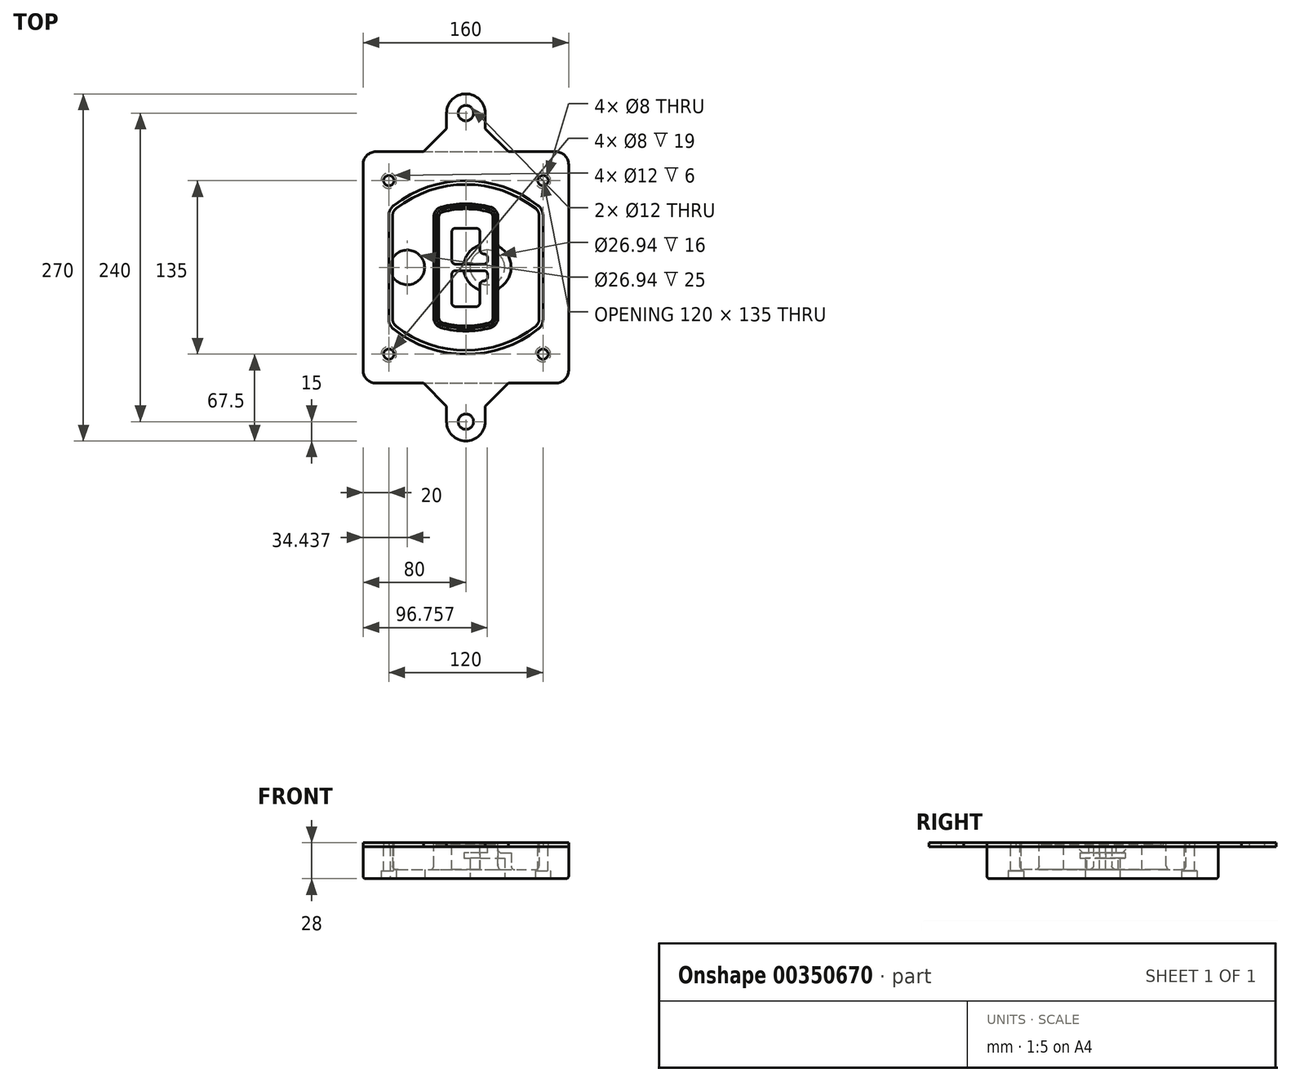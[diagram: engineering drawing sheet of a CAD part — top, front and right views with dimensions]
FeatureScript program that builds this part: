
annotation { "Feature Type Name" : "Feature", "Feature Type Description" : "" }
export const myFeature = defineFeature(function(context is Context, id is Id, definition is map)
    precondition{}
    {
        {
            var Q0;
            Q0=qCreatedBy(makeId("Top.planeOp"),FACE);
            var sketch = newSketch(context, id + "F0", { "sketchPlane" : qUnion([Q0])});
            skPoint(sketch, "E0.rect.middle", {"position": v(0, 0) * mm});
            skLineSegment(sketch, "E1.bottom", {"start": v(-70, -90) * mm, "end": v(70, -90) * mm});
            skLineSegment(sketch, "E1.top", {"start": v(-70, 90) * mm, "end": v(70, 90) * mm});
            skLineSegment(sketch, "E1.left", {"start": v(-80, -80) * mm, "end": v(-80, 80) * mm});
            skLineSegment(sketch, "E1.right", {"start": v(80, -80) * mm, "end": v(80, 80) * mm});
            skLineSegment(sketch, "E2", {"start": v(-80, 90) * mm, "end": v(80, -90) * mm, "construction": true});
            skLineSegment(sketch, "E3", {"start": v(80, 90) * mm, "end": v(-80, -90) * mm, "construction": true});
            skCircle(sketch, "E4", {"center": v(-60, 67.5) * mm, "radius": 4 * mm});
            skCircle(sketch, "E5", {"center": v(60, 67.5) * mm, "radius": 4 * mm});
            skCircle(sketch, "E6", {"center": v(60, -67.5) * mm, "radius": 4 * mm});
            skCircle(sketch, "E7", {"center": v(-60, -67.5) * mm, "radius": 4 * mm});
            skLineSegment(sketch, "E8", {"start": v(-60, 67.5) * mm, "end": v(60, 67.5) * mm, "construction": true});
            skLineSegment(sketch, "E9", {"start": v(60, 67.5) * mm, "end": v(60, -67.5) * mm, "construction": true});
            skLineSegment(sketch, "E10", {"start": v(60, -67.5) * mm, "end": v(-60, -67.5) * mm, "construction": true});
            skLineSegment(sketch, "E11", {"start": v(-60, -67.5) * mm, "end": v(-60, 67.5) * mm, "construction": true});
            skLineSegment(sketch, "E12", {"start": v(-60, 40.3) * mm, "end": v(-60, -40.3) * mm});
            skLineSegment(sketch, "E13", {"start": v(60, 40.3) * mm, "end": v(60, -40.3) * mm});
            skArc(sketch, "E14", {"start": v(56.15, 48.18) * mm, "mid": v(0, 67.5) * mm, "end": v(-56.15, 48.18) * mm});
            skArc(sketch, "E15", {"start": v(-56.15, -48.18) * mm, "mid": v(0, -67.5) * mm, "end": v(56.15, -48.18) * mm});
            skLineSegment(sketch, "E16", {"start": v(-60, 0) * mm, "end": v(60, 0) * mm, "construction": true});
            skPoint(sketch, "E17.visualSharp", {"position": v(-60, -45) * mm});
            skArc(sketch, "E17.filletArc", {"start": v(-60, -40.3) * mm, "mid": v(-58.99, -44.68) * mm, "end": v(-56.15, -48.18) * mm});
            skPoint(sketch, "E18.visualSharp", {"position": v(-60, 45) * mm});
            skArc(sketch, "E18.filletArc", {"start": v(-56.15, 48.18) * mm, "mid": v(-58.99, 44.68) * mm, "end": v(-60, 40.3) * mm});
            skPoint(sketch, "E19.visualSharp", {"position": v(60, 45) * mm});
            skArc(sketch, "E19.filletArc", {"start": v(60, 40.3) * mm, "mid": v(58.99, 44.68) * mm, "end": v(56.15, 48.18) * mm});
            skPoint(sketch, "E20.visualSharp", {"position": v(60, -45) * mm});
            skArc(sketch, "E20.filletArc", {"start": v(56.15, -48.18) * mm, "mid": v(58.99, -44.68) * mm, "end": v(60, -40.3) * mm});
            skPoint(sketch, "E21.visualSharp", {"position": v(-80, 90) * mm});
            skArc(sketch, "E21.filletArc", {"start": v(-70, 90) * mm, "mid": v(-77.07, 87.07) * mm, "end": v(-80, 80) * mm});
            skPoint(sketch, "E22.visualSharp", {"position": v(80, 90) * mm});
            skArc(sketch, "E22.filletArc", {"start": v(80, 80) * mm, "mid": v(77.07, 87.07) * mm, "end": v(70, 90) * mm});
            skPoint(sketch, "E23.visualSharp", {"position": v(80, -90) * mm});
            skArc(sketch, "E23.filletArc", {"start": v(70, -90) * mm, "mid": v(77.07, -87.07) * mm, "end": v(80, -80) * mm});
            skPoint(sketch, "E24.visualSharp", {"position": v(-80, -90) * mm});
            skArc(sketch, "E24.filletArc", {"start": v(-80, -80) * mm, "mid": v(-77.07, -87.07) * mm, "end": v(-70, -90) * mm});
            skArc(sketch, "E25.0", {"start": v(57, 40.3) * mm, "mid": v(56.3, 43.36) * mm, "end": v(54.3, 45.81) * mm});
            skLineSegment(sketch, "E25.1", {"start": v(57, 40.3) * mm, "end": v(57, -40.3) * mm});
            skArc(sketch, "E25.2", {"start": v(54.3, -45.81) * mm, "mid": v(56.3, -43.36) * mm, "end": v(57, -40.3) * mm});
            skArc(sketch, "E25.3", {"start": v(-54.3, -45.81) * mm, "mid": v(0, -64.5) * mm, "end": v(54.3, -45.81) * mm});
            skArc(sketch, "E25.4", {"start": v(-57, -40.3) * mm, "mid": v(-56.3, -43.36) * mm, "end": v(-54.3, -45.81) * mm});
            skArc(sketch, "E25.5", {"start": v(54.3, 45.81) * mm, "mid": v(0, 64.5) * mm, "end": v(-54.3, 45.81) * mm});
            skLineSegment(sketch, "E25.6", {"start": v(-57, 40.3) * mm, "end": v(-57, -40.3) * mm});
            skArc(sketch, "E25.7", {"start": v(-54.3, 45.81) * mm, "mid": v(-56.3, 43.36) * mm, "end": v(-57, 40.3) * mm});
            skArc(sketch, "E26.0", {"start": v(-58.62, 51.33) * mm, "mid": v(-62.58, 46.43) * mm, "end": v(-64, 40.3) * mm});
            skArc(sketch, "E26.1", {"start": v(58.62, 51.33) * mm, "mid": v(0, 71.5) * mm, "end": v(-58.62, 51.33) * mm});
            skArc(sketch, "E26.2", {"start": v(64, 40.3) * mm, "mid": v(62.58, 46.43) * mm, "end": v(58.62, 51.33) * mm});
            skLineSegment(sketch, "E26.3", {"start": v(64, 40.3) * mm, "end": v(64, -40.3) * mm});
            skArc(sketch, "E26.4", {"start": v(58.62, -51.33) * mm, "mid": v(62.58, -46.43) * mm, "end": v(64, -40.3) * mm});
            skLineSegment(sketch, "E26.5", {"start": v(-64, 40.3) * mm, "end": v(-64, -40.3) * mm});
            skArc(sketch, "E26.6", {"start": v(-58.62, -51.33) * mm, "mid": v(0, -71.5) * mm, "end": v(58.62, -51.33) * mm});
            skArc(sketch, "E26.7", {"start": v(-64, -40.3) * mm, "mid": v(-62.58, -46.43) * mm, "end": v(-58.62, -51.33) * mm});
            skSolve(sketch);
        }
        {
            var Q0;
            Q0=makeQuery(id+"F0.imprint","IMPRINT",FACE,{"disambiguationData":[TD([[makeQuery(id+"F0.imprint","IMPRINT",EDGE,{"derivedFrom":sQuery(id+"F0.wireOp",EDGE,"E1.bottom")}),1.0]])]});
            var Q1;
            Q1=makeQuery(id+"F0.imprint","IMPRINT",FACE,{"disambiguationData":[TD([[makeQuery(id+"F0.imprint","IMPRINT",EDGE,{"derivedFrom":sQuery(id+"F0.wireOp",EDGE,"E12")}),1.0]])]});
            var Q2;
            Q2=makeQuery(id+"F0.imprint","IMPRINT",FACE,{"disambiguationData":[TD([[makeQuery(id+"F0.imprint","IMPRINT",EDGE,{"derivedFrom":sQuery(id+"F0.wireOp",EDGE,"E25.0")}),1.0]])]});
            var Q3;
            Q3=makeQuery(id+"F0.imprint","IMPRINT",FACE,{"disambiguationData":[TD([[makeQuery(id+"F0.imprint","IMPRINT",EDGE,{"derivedFrom":sQuery(id+"F0.wireOp",EDGE,"E12")}),-1.0]])]});
            extrude(context, id + "F1", {"entities" : qUnion([Q0, Q1, Q2, Q3]), "oppositeDirection" : true, "depth" : 25 * mm});
        }
        {
            var Q0;
            Q0=makeQuery(id+"F0.imprint","IMPRINT",FACE,{"disambiguationData":[TD([[makeQuery(id+"F0.imprint","IMPRINT",EDGE,{"derivedFrom":sQuery(id+"F0.wireOp",EDGE,"E12")}),1.0]])]});
            extrude(context, id + "F2", {"entities" : qUnion([Q0]), "operationType" : NewBodyOperationType.ADD, "depth" : 3 * mm});
        }
        {
            var Q0;
            Q0=makeQuery(id+"F0.imprint","IMPRINT",FACE,{"disambiguationData":[TD([[makeQuery(id+"F0.imprint","IMPRINT",EDGE,{"derivedFrom":sQuery(id+"F0.wireOp",EDGE,"E25.0")}),1.0]])]});
            extrude(context, id + "F3", {"entities" : qUnion([Q0]), "operationType" : NewBodyOperationType.REMOVE, "oppositeDirection" : true, "depth" : 18 * mm});
        }
        {
            var Q0;
            Q0=makeQuery(id+"F2.opExtrude","CAP_FACE",FACE,{"disambiguationData":[OSD([sQuery(id+"F0.wireOp",EDGE,"E12"),sQuery(id+"F0.wireOp",EDGE,"E13"),sQuery(id+"F0.wireOp",EDGE,"E14"),sQuery(id+"F0.wireOp",EDGE,"E15"),sQuery(id+"F0.wireOp",EDGE,"E17.filletArc"),sQuery(id+"F0.wireOp",EDGE,"E18.filletArc"),sQuery(id+"F0.wireOp",EDGE,"E19.filletArc"),sQuery(id+"F0.wireOp",EDGE,"E20.filletArc"),sQuery(id+"F0.wireOp",EDGE,"E25.0"),sQuery(id+"F0.wireOp",EDGE,"E25.1"),sQuery(id+"F0.wireOp",EDGE,"E25.2"),sQuery(id+"F0.wireOp",EDGE,"E25.3"),sQuery(id+"F0.wireOp",EDGE,"E25.4"),sQuery(id+"F0.wireOp",EDGE,"E25.5"),sQuery(id+"F0.wireOp",EDGE,"E25.6"),sQuery(id+"F0.wireOp",EDGE,"E25.7")])],"isStart":false});
            var sketch = newSketch(context, id + "F4", { "sketchPlane" : qUnion([Q0])});
            skArc(sketch, "E27.0", {"start": v(-19.08, -46.97) * mm, "mid": v(0, -49.5) * mm, "end": v(19.08, -46.97) * mm});
            skArc(sketch, "E28.0", {"start": v(19.08, 46.97) * mm, "mid": v(0, 49.5) * mm, "end": v(-19.08, 46.97) * mm});
            skLineSegment(sketch, "E29", {"start": v(-25, 39.25) * mm, "end": v(-25, -39.25) * mm});
            skLineSegment(sketch, "E30", {"start": v(25, 39.25) * mm, "end": v(25, -39.25) * mm});
            skLineSegment(sketch, "E31", {"start": v(-25, 45.1) * mm, "end": v(25, 45.1) * mm, "construction": true});
            skLineSegment(sketch, "E32", {"start": v(-25, -45.1) * mm, "end": v(25, -45.1) * mm, "construction": true});
            skPoint(sketch, "E33.visualSharp", {"position": v(-25, 45.1) * mm});
            skArc(sketch, "E33.filletArc", {"start": v(-19.08, 46.97) * mm, "mid": v(-23.35, 44.11) * mm, "end": v(-25, 39.25) * mm});
            skPoint(sketch, "E34.visualSharp", {"position": v(25, 45.1) * mm});
            skArc(sketch, "E34.filletArc", {"start": v(25, 39.25) * mm, "mid": v(23.35, 44.11) * mm, "end": v(19.08, 46.97) * mm});
            skPoint(sketch, "E35.visualSharp", {"position": v(25, -45.1) * mm});
            skArc(sketch, "E35.filletArc", {"start": v(19.08, -46.97) * mm, "mid": v(23.35, -44.11) * mm, "end": v(25, -39.25) * mm});
            skPoint(sketch, "E36.visualSharp", {"position": v(-25, -45.1) * mm});
            skArc(sketch, "E36.filletArc", {"start": v(-25, -39.25) * mm, "mid": v(-23.35, -44.11) * mm, "end": v(-19.08, -46.97) * mm});
            skArc(sketch, "E37.0", {"start": v(54.3, 45.81) * mm, "mid": v(0, 64.5) * mm, "end": v(-54.3, 45.81) * mm});
            skArc(sketch, "E37.1", {"start": v(-54.3, 45.81) * mm, "mid": v(-56.3, 43.36) * mm, "end": v(-57, 40.3) * mm});
            skLineSegment(sketch, "E37.2", {"start": v(-57, 40.3) * mm, "end": v(-57, -40.3) * mm});
            skArc(sketch, "E37.3", {"start": v(-57, -40.3) * mm, "mid": v(-56.3, -43.36) * mm, "end": v(-54.3, -45.81) * mm});
            skArc(sketch, "E37.4", {"start": v(-54.3, -45.81) * mm, "mid": v(0, -64.5) * mm, "end": v(54.3, -45.81) * mm});
            skArc(sketch, "E37.5", {"start": v(54.3, -45.81) * mm, "mid": v(56.3, -43.36) * mm, "end": v(57, -40.3) * mm});
            skLineSegment(sketch, "E37.6", {"start": v(57, 40.3) * mm, "end": v(57, -40.3) * mm});
            skArc(sketch, "E37.7", {"start": v(57, 40.3) * mm, "mid": v(56.3, 43.36) * mm, "end": v(54.3, 45.81) * mm});
            skLineSegment(sketch, "E38.0", {"start": v(23, 39.25) * mm, "end": v(23, -39.25) * mm});
            skArc(sketch, "E38.1", {"start": v(18.56, -45.04) * mm, "mid": v(21.76, -42.9) * mm, "end": v(23, -39.25) * mm});
            skArc(sketch, "E38.2", {"start": v(-18.56, -45.04) * mm, "mid": v(0, -47.5) * mm, "end": v(18.56, -45.04) * mm});
            skArc(sketch, "E38.3", {"start": v(-23, -39.25) * mm, "mid": v(-21.76, -42.9) * mm, "end": v(-18.56, -45.04) * mm});
            skLineSegment(sketch, "E38.4", {"start": v(-23, 39.25) * mm, "end": v(-23, -39.25) * mm});
            skArc(sketch, "E38.5", {"start": v(23, 39.25) * mm, "mid": v(21.76, 42.9) * mm, "end": v(18.56, 45.04) * mm});
            skArc(sketch, "E38.6", {"start": v(-18.56, 45.04) * mm, "mid": v(-21.76, 42.9) * mm, "end": v(-23, 39.25) * mm});
            skArc(sketch, "E38.7", {"start": v(18.56, 45.04) * mm, "mid": v(0, 47.5) * mm, "end": v(-18.56, 45.04) * mm});
            skArc(sketch, "E39.0", {"start": v(21, 39.25) * mm, "mid": v(20.18, 41.68) * mm, "end": v(18.04, 43.1) * mm});
            skLineSegment(sketch, "E39.1", {"start": v(21, 39.25) * mm, "end": v(21, -39.25) * mm});
            skArc(sketch, "E39.2", {"start": v(18.04, -43.1) * mm, "mid": v(20.18, -41.68) * mm, "end": v(21, -39.25) * mm});
            skArc(sketch, "E39.3", {"start": v(-18.04, -43.1) * mm, "mid": v(0, -45.5) * mm, "end": v(18.04, -43.1) * mm});
            skArc(sketch, "E39.4", {"start": v(-21, -39.25) * mm, "mid": v(-20.18, -41.68) * mm, "end": v(-18.04, -43.1) * mm});
            skArc(sketch, "E39.5", {"start": v(18.04, 43.1) * mm, "mid": v(0, 45.5) * mm, "end": v(-18.04, 43.1) * mm});
            skLineSegment(sketch, "E39.6", {"start": v(-21, 39.25) * mm, "end": v(-21, -39.25) * mm});
            skArc(sketch, "E39.7", {"start": v(-18.04, 43.1) * mm, "mid": v(-20.18, 41.68) * mm, "end": v(-21, 39.25) * mm});
            skLineSegment(sketch, "E40", {"start": v(-25, 0) * mm, "end": v(25, 0) * mm, "construction": true});
            skLineSegment(sketch, "E41", {"start": v(-11, 5.5) * mm, "end": v(-11, 27.5) * mm});
            skLineSegment(sketch, "E42", {"start": v(-8, 30.5) * mm, "end": v(8, 30.5) * mm});
            skLineSegment(sketch, "E43", {"start": v(11, 27.5) * mm, "end": v(11, 13.5) * mm});
            skLineSegment(sketch, "E44", {"start": v(14, 10.5) * mm, "end": v(14, 10.5) * mm});
            skLineSegment(sketch, "E45", {"start": v(17, 7.5) * mm, "end": v(17, 5.5) * mm});
            skLineSegment(sketch, "E46", {"start": v(14, 2.5) * mm, "end": v(-8, 2.5) * mm});
            skPoint(sketch, "E47.visualSharp", {"position": v(-11, 30.5) * mm});
            skArc(sketch, "E47.filletArc", {"start": v(-8, 30.5) * mm, "mid": v(-10.12, 29.62) * mm, "end": v(-11, 27.5) * mm});
            skPoint(sketch, "E48.visualSharp", {"position": v(11, 30.5) * mm});
            skArc(sketch, "E48.filletArc", {"start": v(11, 27.5) * mm, "mid": v(10.12, 29.62) * mm, "end": v(8, 30.5) * mm});
            skPoint(sketch, "E49.visualSharp", {"position": v(11, 10.5) * mm});
            skArc(sketch, "E49.filletArc", {"start": v(11, 13.5) * mm, "mid": v(11.88, 11.38) * mm, "end": v(14, 10.5) * mm});
            skPoint(sketch, "E50.visualSharp", {"position": v(17, 10.5) * mm});
            skArc(sketch, "E50.filletArc", {"start": v(17, 7.5) * mm, "mid": v(16.12, 9.62) * mm, "end": v(14, 10.5) * mm});
            skPoint(sketch, "E51.visualSharp", {"position": v(17, 2.5) * mm});
            skArc(sketch, "E51.filletArc", {"start": v(14, 2.5) * mm, "mid": v(16.12, 3.38) * mm, "end": v(17, 5.5) * mm});
            skPoint(sketch, "E52.visualSharp", {"position": v(-11, 2.5) * mm});
            skArc(sketch, "E52.filletArc", {"start": v(-11, 5.5) * mm, "mid": v(-10.12, 3.38) * mm, "end": v(-8, 2.5) * mm});
            skLineSegment(sketch, "E53.0.MirrorCS", {"start": v(14, -2.5) * mm, "end": v(-8, -2.5) * mm});
            skArc(sketch, "E54.0.MirrorCS", {"start": v(-11, -5.5) * mm, "mid": v(-10.12, -3.38) * mm, "end": v(-8, -2.5) * mm});
            skLineSegment(sketch, "E55.0.MirrorCS", {"start": v(-11, -5.5) * mm, "end": v(-11, -27.5) * mm});
            skArc(sketch, "E56.0.MirrorCS", {"start": v(-8, -30.5) * mm, "mid": v(-10.12, -29.62) * mm, "end": v(-11, -27.5) * mm});
            skLineSegment(sketch, "E57.0.MirrorCS", {"start": v(-8, -30.5) * mm, "end": v(8, -30.5) * mm});
            skArc(sketch, "E58.0.MirrorCS", {"start": v(11, -27.5) * mm, "mid": v(10.12, -29.62) * mm, "end": v(8, -30.5) * mm});
            skLineSegment(sketch, "E59.0.MirrorCS", {"start": v(11, -27.5) * mm, "end": v(11, -13.5) * mm});
            skArc(sketch, "E60.0.MirrorCS", {"start": v(11, -13.5) * mm, "mid": v(11.88, -11.38) * mm, "end": v(14, -10.5) * mm});
            skArc(sketch, "E61.0.MirrorCS", {"start": v(17, -7.5) * mm, "mid": v(16.12, -9.62) * mm, "end": v(14, -10.5) * mm});
            skLineSegment(sketch, "E62.0.MirrorCS", {"start": v(17, -7.5) * mm, "end": v(17, -5.5) * mm});
            skArc(sketch, "E63.0.MirrorCS", {"start": v(14, -2.5) * mm, "mid": v(16.12, -3.38) * mm, "end": v(17, -5.5) * mm});
            skSolve(sketch);
        }
        {
            var Q0;
            Q0=makeQuery(id+"F4.imprint","IMPRINT",FACE,{"disambiguationData":[TD([[makeQuery(id+"F4.imprint","IMPRINT",EDGE,{"derivedFrom":sQuery(id+"F4.wireOp",EDGE,"E27.0")}),1.0]])]});
            var Q1;
            Q1=makeQuery(id+"F4.imprint","IMPRINT",FACE,{"disambiguationData":[TD([[makeQuery(id+"F4.imprint","IMPRINT",EDGE,{"derivedFrom":sQuery(id+"F4.wireOp",EDGE,"E38.0")}),-1.0]])]});
            var Q2;
            Q2=makeQuery(id+"F4.imprint","IMPRINT",FACE,{"disambiguationData":[TD([[makeQuery(id+"F4.imprint","IMPRINT",EDGE,{"derivedFrom":sQuery(id+"F4.wireOp",EDGE,"E39.0")}),1.0]])]});
            extrude(context, id + "F5", {"entities" : qUnion([Q0, Q1, Q2]), "operationType" : NewBodyOperationType.ADD, "endBound" : BoundingType.UP_TO_NEXT, "oppositeDirection" : true, "depth" : 25 * mm});
        }
        {
            var Q0;
            Q0=makeQuery(id+"F4.imprint","IMPRINT",FACE,{"disambiguationData":[TD([[makeQuery(id+"F4.imprint","IMPRINT",EDGE,{"derivedFrom":sQuery(id+"F4.wireOp",EDGE,"E38.0")}),-1.0]])]});
            extrude(context, id + "F6", {"entities" : qUnion([Q0]), "operationType" : NewBodyOperationType.REMOVE, "oppositeDirection" : true, "depth" : 2 * mm});
        }
        {
            var Q0;
            Q0=makeQuery(id+"F1.opExtrude","CAP_FACE",FACE,{"disambiguationData":[OSD([sQuery(id+"F0.wireOp",EDGE,"E1.bottom"),sQuery(id+"F0.wireOp",EDGE,"E1.top"),sQuery(id+"F0.wireOp",EDGE,"E1.left"),sQuery(id+"F0.wireOp",EDGE,"E1.right"),sQuery(id+"F0.wireOp",EDGE,"E4"),sQuery(id+"F0.wireOp",EDGE,"E5"),sQuery(id+"F0.wireOp",EDGE,"E6"),sQuery(id+"F0.wireOp",EDGE,"E7"),sQuery(id+"F0.wireOp",EDGE,"E21.filletArc"),sQuery(id+"F0.wireOp",EDGE,"E22.filletArc"),sQuery(id+"F0.wireOp",EDGE,"E23.filletArc"),sQuery(id+"F0.wireOp",EDGE,"E24.filletArc")])],"isStart":false});
            var sketch = newSketch(context, id + "F7", { "sketchPlane" : qUnion([Q0])});
            skCircle(sketch, "E64", {"center": v(16.76, 0) * mm, "radius": 13.47 * mm});
            skCircle(sketch, "E65", {"center": v(-45.56, 0) * mm, "radius": 13.47 * mm});
            skLineSegment(sketch, "E66", {"start": v(80, 0) * mm, "end": v(-80, 0) * mm});
            skCircle(sketch, "E67", {"center": v(16.76, 0) * mm, "radius": 18.47 * mm});
            skCircle(sketch, "E68", {"center": v(60, -67.5) * mm, "radius": 6 * mm});
            skCircle(sketch, "E69", {"center": v(-60, -67.5) * mm, "radius": 6 * mm});
            skCircle(sketch, "E70", {"center": v(-60, 67.5) * mm, "radius": 6 * mm});
            skCircle(sketch, "E71", {"center": v(60, 67.5) * mm, "radius": 6 * mm});
            skSolve(sketch);
        }
        {
            var Q0;
            {var subQ1=sQuery(id+"F7.wireOp",EDGE,"E66");var subQ4=sQuery(id+"F7.wireOp",EDGE,"E64");var subQ6=makeQuery(id+"F7.imprint","INTERSECT",VERTEX,{"disambiguationData":[OD(0.0)],"derivedFrom":[subQ4,subQ1]});Q0=makeQuery(id+"F7.imprint","IMPRINT",FACE,{"disambiguationData":[TD([[makeQuery(id+"F7.imprint","IMPRINT",EDGE,{"disambiguationData":[TD([[subQ6,-1.0]])],"derivedFrom":subQ4}),-1.0]])]});}
            var Q1;
            {var subQ0=sQuery(id+"F7.wireOp",EDGE,"E66");var subQ1=sQuery(id+"F7.wireOp",EDGE,"E64");var subQ3=makeQuery(id+"F7.imprint","INTERSECT",VERTEX,{"disambiguationData":[OD(0.0)],"derivedFrom":[subQ1,subQ0]});Q1=makeQuery(id+"F7.imprint","IMPRINT",FACE,{"disambiguationData":[TD([[makeQuery(id+"F7.imprint","IMPRINT",EDGE,{"disambiguationData":[TD([[subQ3,-1.0]])],"derivedFrom":subQ1}),1.0]])]});}
            var Q2;
            {var subQ0=sQuery(id+"F7.wireOp",EDGE,"E66");var subQ1=sQuery(id+"F7.wireOp",EDGE,"E64");var subQ3=makeQuery(id+"F7.imprint","INTERSECT",VERTEX,{"disambiguationData":[OD(0.0)],"derivedFrom":[subQ1,subQ0]});Q2=makeQuery(id+"F7.imprint","IMPRINT",FACE,{"disambiguationData":[TD([[makeQuery(id+"F7.imprint","IMPRINT",EDGE,{"disambiguationData":[TD([[subQ3,1.0]])],"derivedFrom":subQ1}),1.0]])]});}
            var Q3;
            {var subQ1=sQuery(id+"F7.wireOp",EDGE,"E66");var subQ4=sQuery(id+"F7.wireOp",EDGE,"E64");var subQ6=makeQuery(id+"F7.imprint","INTERSECT",VERTEX,{"disambiguationData":[OD(0.0)],"derivedFrom":[subQ4,subQ1]});Q3=makeQuery(id+"F7.imprint","IMPRINT",FACE,{"disambiguationData":[TD([[makeQuery(id+"F7.imprint","IMPRINT",EDGE,{"disambiguationData":[TD([[subQ6,1.0]])],"derivedFrom":subQ4}),-1.0]])]});}
            extrude(context, id + "F8", {"entities" : qUnion([Q0, Q1, Q2, Q3]), "operationType" : NewBodyOperationType.ADD, "oppositeDirection" : true, "depth" : 20 * mm});
        }
        {
            var Q0;
            {var subQ0=sQuery(id+"F7.wireOp",EDGE,"E66");var subQ1=sQuery(id+"F7.wireOp",EDGE,"E64");var subQ3=makeQuery(id+"F7.imprint","INTERSECT",VERTEX,{"disambiguationData":[OD(0.0)],"derivedFrom":[subQ1,subQ0]});Q0=makeQuery(id+"F7.imprint","IMPRINT",FACE,{"disambiguationData":[TD([[makeQuery(id+"F7.imprint","IMPRINT",EDGE,{"disambiguationData":[TD([[subQ3,-1.0]])],"derivedFrom":subQ1}),1.0]])]});}
            var Q1;
            {var subQ0=sQuery(id+"F7.wireOp",EDGE,"E66");var subQ1=sQuery(id+"F7.wireOp",EDGE,"E64");var subQ3=makeQuery(id+"F7.imprint","INTERSECT",VERTEX,{"disambiguationData":[OD(0.0)],"derivedFrom":[subQ1,subQ0]});Q1=makeQuery(id+"F7.imprint","IMPRINT",FACE,{"disambiguationData":[TD([[makeQuery(id+"F7.imprint","IMPRINT",EDGE,{"disambiguationData":[TD([[subQ3,1.0]])],"derivedFrom":subQ1}),1.0]])]});}
            extrude(context, id + "F9", {"entities" : qUnion([Q0, Q1]), "operationType" : NewBodyOperationType.REMOVE, "oppositeDirection" : true, "depth" : 16 * mm});
        }
        {
            var Q0;
            Q0=makeQuery(id+"F7.imprint","IMPRINT",FACE,{"disambiguationData":[TD([[makeQuery(id+"F7.imprint","IMPRINT",EDGE,{"derivedFrom":sQuery(id+"F7.wireOp",EDGE,"E68")}),1.0]])]});
            var Q1;
            Q1=makeQuery(id+"F7.imprint","IMPRINT",FACE,{"disambiguationData":[TD([[makeQuery(id+"F7.imprint","IMPRINT",EDGE,{"derivedFrom":makeQuery(id+"F1.opExtrude","CAP_EDGE",EDGE,{"disambiguationData":[OSD([sQuery(id+"F0.wireOp",EDGE,"E5")])],"isStart":false})}),-1.0]])]});
            var Q2;
            Q2=makeQuery(id+"F7.imprint","IMPRINT",FACE,{"disambiguationData":[TD([[makeQuery(id+"F7.imprint","IMPRINT",EDGE,{"derivedFrom":sQuery(id+"F7.wireOp",EDGE,"E69")}),1.0]])]});
            var Q3;
            Q3=makeQuery(id+"F7.imprint","IMPRINT",FACE,{"disambiguationData":[TD([[makeQuery(id+"F7.imprint","IMPRINT",EDGE,{"derivedFrom":makeQuery(id+"F1.opExtrude","CAP_EDGE",EDGE,{"disambiguationData":[OSD([sQuery(id+"F0.wireOp",EDGE,"E4")])],"isStart":false})}),-1.0]])]});
            var Q4;
            Q4=makeQuery(id+"F7.imprint","IMPRINT",FACE,{"disambiguationData":[TD([[makeQuery(id+"F7.imprint","IMPRINT",EDGE,{"derivedFrom":sQuery(id+"F7.wireOp",EDGE,"E70")}),1.0]])]});
            var Q5;
            Q5=makeQuery(id+"F7.imprint","IMPRINT",FACE,{"disambiguationData":[TD([[makeQuery(id+"F7.imprint","IMPRINT",EDGE,{"derivedFrom":makeQuery(id+"F1.opExtrude","CAP_EDGE",EDGE,{"disambiguationData":[OSD([sQuery(id+"F0.wireOp",EDGE,"E7")])],"isStart":false})}),-1.0]])]});
            var Q6;
            Q6=makeQuery(id+"F7.imprint","IMPRINT",FACE,{"disambiguationData":[TD([[makeQuery(id+"F7.imprint","IMPRINT",EDGE,{"derivedFrom":sQuery(id+"F7.wireOp",EDGE,"E71")}),1.0]])]});
            var Q7;
            Q7=makeQuery(id+"F7.imprint","IMPRINT",FACE,{"disambiguationData":[TD([[makeQuery(id+"F7.imprint","IMPRINT",EDGE,{"derivedFrom":makeQuery(id+"F1.opExtrude","CAP_EDGE",EDGE,{"disambiguationData":[OSD([sQuery(id+"F0.wireOp",EDGE,"E6")])],"isStart":false})}),-1.0]])]});
            extrude(context, id + "F10", {"entities" : qUnion([Q0, Q1, Q2, Q3, Q4, Q5, Q6, Q7]), "operationType" : NewBodyOperationType.REMOVE, "oppositeDirection" : true, "depth" : 6 * mm});
        }
        {
            var Q0;
            {var subQ0=sQuery(id+"F7.wireOp",EDGE,"E66");var subQ1=sQuery(id+"F7.wireOp",EDGE,"E65");var subQ3=makeQuery(id+"F7.imprint","INTERSECT",VERTEX,{"disambiguationData":[OD(0.0)],"derivedFrom":[subQ1,subQ0]});Q0=makeQuery(id+"F7.imprint","IMPRINT",FACE,{"disambiguationData":[TD([[makeQuery(id+"F7.imprint","IMPRINT",EDGE,{"disambiguationData":[TD([[subQ3,-1.0]])],"derivedFrom":subQ1}),1.0]])]});}
            var Q1;
            {var subQ0=sQuery(id+"F7.wireOp",EDGE,"E66");var subQ1=sQuery(id+"F7.wireOp",EDGE,"E65");var subQ3=makeQuery(id+"F7.imprint","INTERSECT",VERTEX,{"disambiguationData":[OD(0.0)],"derivedFrom":[subQ1,subQ0]});Q1=makeQuery(id+"F7.imprint","IMPRINT",FACE,{"disambiguationData":[TD([[makeQuery(id+"F7.imprint","IMPRINT",EDGE,{"disambiguationData":[TD([[subQ3,1.0]])],"derivedFrom":subQ1}),1.0]])]});}
            extrude(context, id + "F11", {"entities" : qUnion([Q0, Q1]), "operationType" : NewBodyOperationType.REMOVE, "oppositeDirection" : true, "depth" : 25 * mm});
        }
        {
            var Q0;
            Q0=makeQuery(id+"F9.boolean.opBoolean","COPY",FACE,{"derivedFrom":makeQuery(id+"F9.opExtrude","CAP_FACE",FACE,{"disambiguationData":[OSD([sQuery(id+"F7.wireOp",EDGE,"E64")])],"isStart":false})});
            var sketch = newSketch(context, id + "F12", { "sketchPlane" : qUnion([Q0])});
            skArc(sketch, "E72.0", {"start": v(11, 17.55) * mm, "mid": v(2.57, 11.82) * mm, "end": v(-1.54, 2.5) * mm});
            skArc(sketch, "E72.1", {"start": v(-1.54, -2.5) * mm, "mid": v(2.57, -11.82) * mm, "end": v(11, -17.55) * mm});
            skLineSegment(sketch, "E73", {"start": v(-1.54, -2.5) * mm, "end": v(14, -2.5) * mm});
            skLineSegment(sketch, "E74.0", {"start": v(14, 2.5) * mm, "end": v(-1.54, 2.5) * mm});
            skArc(sketch, "E74.1", {"start": v(14, 2.5) * mm, "mid": v(16.12, 3.38) * mm, "end": v(17, 5.5) * mm});
            skLineSegment(sketch, "E74.2", {"start": v(17, 7.5) * mm, "end": v(17, 5.5) * mm});
            skArc(sketch, "E74.3", {"start": v(17, 7.5) * mm, "mid": v(16.12, 9.62) * mm, "end": v(14, 10.5) * mm});
            skArc(sketch, "E74.4", {"start": v(11, 13.5) * mm, "mid": v(11.88, 11.38) * mm, "end": v(14, 10.5) * mm});
            skLineSegment(sketch, "E74.5", {"start": v(11, 17.55) * mm, "end": v(11, 13.5) * mm});
            skLineSegment(sketch, "E74.7", {"start": v(14, -2.5) * mm, "end": v(-1.54, -2.5) * mm});
            skArc(sketch, "E74.8", {"start": v(14, -2.5) * mm, "mid": v(16.12, -3.38) * mm, "end": v(17, -5.5) * mm});
            skLineSegment(sketch, "E74.9", {"start": v(17, -7.5) * mm, "end": v(17, -5.5) * mm});
            skArc(sketch, "E74.10", {"start": v(17, -7.5) * mm, "mid": v(16.12, -9.62) * mm, "end": v(14, -10.5) * mm});
            skArc(sketch, "E74.11", {"start": v(11, -13.5) * mm, "mid": v(11.88, -11.38) * mm, "end": v(14, -10.5) * mm});
            skLineSegment(sketch, "E74.12", {"start": v(11, -17.55) * mm, "end": v(11, -13.5) * mm});
            skPoint(sketch, "E75.orphan", {"position": v(11, -27.5) * mm});
            skPoint(sketch, "E76.orphan", {"position": v(-8, -2.5) * mm});
            skPoint(sketch, "E77.orphan", {"position": v(-8, 2.5) * mm});
            skPoint(sketch, "E78.orphan", {"position": v(11, 27.5) * mm});
            skSolve(sketch);
        }
        {
            var Q0;
            {var subQ7=sQuery(id+"F12.wireOp",EDGE,"E72.0");var subQ14=sQuery(id+"F12.wireOp",EDGE,"E72.1");var subQ16=sQuery(id+"F12.wireOp",EDGE,"E74.1");var subQ18=sQuery(id+"F12.wireOp",EDGE,"E74.8");Q0=qUnion([makeQuery(id+"F12.imprint","IMPRINT",FACE,{"disambiguationData":[TD([[makeQuery(id+"F12.imprint","IMPRINT",EDGE,{"derivedFrom":subQ7}),1.0]])]}),makeQuery(id+"F12.imprint","IMPRINT",FACE,{"disambiguationData":[TD([[makeQuery(id+"F12.imprint","IMPRINT",EDGE,{"derivedFrom":subQ14}),1.0]])]}),makeQuery(id+"F12.imprint","IMPRINT",FACE,{"disambiguationData":[TD([[makeQuery(id+"F12.imprint","IMPRINT",EDGE,{"derivedFrom":subQ16}),1.0]])]}),makeQuery(id+"F12.imprint","IMPRINT",FACE,{"disambiguationData":[TD([[makeQuery(id+"F12.imprint","IMPRINT",EDGE,{"derivedFrom":subQ18}),-1.0]])]})]);}
            var Q1;
            Q1=makeQuery(id+"F5.boolean.opBoolean","SPLIT",FACE,{"disambiguationData":[TD([makeQuery(id+"F5.opExtrude","SWEPT_FACE",FACE,{"disambiguationData":[OSD([sQuery(id+"F4.wireOp",EDGE,"E41")])]})])],"derivedFrom":makeQuery(id+"F3.boolean.opBoolean","COPY",FACE,{"derivedFrom":makeQuery(id+"F3.opExtrude","CAP_FACE",FACE,{"disambiguationData":[OSD([sQuery(id+"F0.wireOp",EDGE,"E25.0"),sQuery(id+"F0.wireOp",EDGE,"E25.1"),sQuery(id+"F0.wireOp",EDGE,"E25.2"),sQuery(id+"F0.wireOp",EDGE,"E25.3"),sQuery(id+"F0.wireOp",EDGE,"E25.4"),sQuery(id+"F0.wireOp",EDGE,"E25.5"),sQuery(id+"F0.wireOp",EDGE,"E25.6"),sQuery(id+"F0.wireOp",EDGE,"E25.7")])],"isStart":false})})});
            extrude(context, id + "F13", {"entities" : qUnion([Q0]), "operationType" : NewBodyOperationType.REMOVE, "endBound" : BoundingType.UP_TO_SURFACE, "endBoundEntityFace" : qUnion([Q1]), "depth" : 25 * mm});
        }
        {
            var Q0;
            Q0=makeQuery(id+"F3.boolean.opBoolean","COPY",EDGE,{"derivedFrom":makeQuery(id+"F3.opExtrude","CAP_EDGE",EDGE,{"disambiguationData":[OSD([sQuery(id+"F0.wireOp",EDGE,"E25.6")])],"isStart":false})});
            var Q1;
            Q1=makeQuery(id+"F8.boolean.opBoolean","INTERSECT",EDGE,{"derivedFrom":[makeQuery(id+"F5.opExtrude","SWEPT_FACE",FACE,{"disambiguationData":[OSD([sQuery(id+"F4.wireOp",EDGE,"E30")])]}),makeQuery(id+"F8.opExtrude","CAP_FACE",FACE,{"disambiguationData":[OSD([sQuery(id+"F7.wireOp",EDGE,"E67")])],"isStart":false})]});
            var Q2;
            Q2=makeQuery(id+"F8.boolean.opBoolean","INTERSECT",EDGE,{"disambiguationData":[OD(1.0)],"derivedFrom":[makeQuery(id+"F5.opExtrude","SWEPT_FACE",FACE,{"disambiguationData":[OSD([sQuery(id+"F4.wireOp",EDGE,"E30")])]}),makeQuery(id+"F8.opExtrude","SWEPT_FACE",FACE,{"disambiguationData":[OSD([sQuery(id+"F7.wireOp",EDGE,"E67")])]})]});
            var Q3;
            {var subQ0=sQuery(id+"F4.wireOp",EDGE,"E30");Q3=makeQuery(id+"F8.boolean.opBoolean","SPLIT",EDGE,{"disambiguationData":[TD([makeQuery(id+"F5.opExtrude","SWEPT_FACE",FACE,{"disambiguationData":[OSD([sQuery(id+"F4.wireOp",EDGE,"E35.filletArc")])]})])],"derivedFrom":makeQuery(id+"F5.opExtrude","CAP_EDGE",EDGE,{"disambiguationData":[OSD([subQ0])],"isStart":false})});}
            var Q4;
            {var subQ0=sQuery(id+"F0.wireOp",EDGE,"E25.7");var subQ1=sQuery(id+"F0.wireOp",EDGE,"E25.1");var subQ2=sQuery(id+"F0.wireOp",EDGE,"E25.6");var subQ3=sQuery(id+"F0.wireOp",EDGE,"E25.5");var subQ4=sQuery(id+"F0.wireOp",EDGE,"E25.4");var subQ5=sQuery(id+"F0.wireOp",EDGE,"E25.0");var subQ6=sQuery(id+"F0.wireOp",EDGE,"E25.2");var subQ7=sQuery(id+"F0.wireOp",EDGE,"E25.3");Q4=makeQuery(id+"F8.boolean.opBoolean","INTERSECT",EDGE,{"derivedFrom":[makeQuery(id+"F5.boolean.opBoolean","SPLIT",FACE,{"disambiguationData":[TD([makeQuery(id+"F2.opExtrude","SWEPT_FACE",FACE,{"disambiguationData":[OSD([subQ5])]})])],"derivedFrom":makeQuery(id+"F3.boolean.opBoolean","COPY",FACE,{"derivedFrom":makeQuery(id+"F3.opExtrude","CAP_FACE",FACE,{"disambiguationData":[OSD([subQ5,subQ1,subQ6,subQ7,subQ4,subQ3,subQ2,subQ0])],"isStart":false})})}),makeQuery(id+"F8.opExtrude","SWEPT_FACE",FACE,{"disambiguationData":[OSD([sQuery(id+"F7.wireOp",EDGE,"E67")])]})]});}
            var Q5;
            Q5=makeQuery(id+"F8.boolean.opBoolean","INTERSECT",EDGE,{"disambiguationData":[OD(0.0)],"derivedFrom":[makeQuery(id+"F5.opExtrude","SWEPT_FACE",FACE,{"disambiguationData":[OSD([sQuery(id+"F4.wireOp",EDGE,"E30")])]}),makeQuery(id+"F8.opExtrude","SWEPT_FACE",FACE,{"disambiguationData":[OSD([sQuery(id+"F7.wireOp",EDGE,"E67")])]})]});
            fillet(context, id + "F14", {"entities" : qUnion([Q0, Q1, Q2, Q3, Q4, Q5]), "radius" : 3 * mm, "tangentPropagation" : true, "allowEdgeOverflow" : false});
        }
        {
            var Q0;
            Q0=makeQuery(id+"F1.opExtrude","CAP_EDGE",EDGE,{"disambiguationData":[OSD([sQuery(id+"F0.wireOp",EDGE,"E1.bottom")])],"isStart":false});
            fillet(context, id + "F15", {"entities" : qUnion([Q0]), "radius" : 2 * mm, "tangentPropagation" : true, "allowEdgeOverflow" : false});
        }
        {
            var Q0;
            {var subQ0=sQuery(id+"F0.wireOp",EDGE,"E21.filletArc");var subQ1=sQuery(id+"F0.wireOp",EDGE,"E7");var subQ2=sQuery(id+"F0.wireOp",EDGE,"E6");var subQ3=sQuery(id+"F0.wireOp",EDGE,"E5");var subQ4=sQuery(id+"F0.wireOp",EDGE,"E4");var subQ5=sQuery(id+"F0.wireOp",EDGE,"E22.filletArc");var subQ6=sQuery(id+"F0.wireOp",EDGE,"E1.bottom");var subQ7=sQuery(id+"F0.wireOp",EDGE,"E1.right");var subQ8=sQuery(id+"F0.wireOp",EDGE,"E1.top");var subQ9=sQuery(id+"F0.wireOp",EDGE,"E1.left");var subQ10=sQuery(id+"F0.wireOp",EDGE,"E23.filletArc");var subQ11=sQuery(id+"F0.wireOp",EDGE,"E24.filletArc");Q0=makeQuery(id+"F2.boolean.opBoolean","SPLIT",FACE,{"disambiguationData":[TD([makeQuery(id+"F1.opExtrude","SWEPT_FACE",FACE,{"disambiguationData":[OSD([subQ6])]})])],"derivedFrom":makeQuery(id+"F1.opExtrude","CAP_FACE",FACE,{"disambiguationData":[OSD([subQ6,subQ8,subQ9,subQ7,subQ4,subQ3,subQ2,subQ1,subQ0,subQ5,subQ10,subQ11])],"isStart":true})});}
            var sketch = newSketch(context, id + "F16", { "sketchPlane" : qUnion([Q0])});
            skLineSegment(sketch, "E79.0", {"start": v(80, -80) * mm, "end": v(80, 80) * mm});
            skLineSegment(sketch, "E79.1", {"start": v(-70, 90) * mm, "end": v(70, 90) * mm});
            skLineSegment(sketch, "E79.2", {"start": v(-70, -90) * mm, "end": v(70, -90) * mm});
            skLineSegment(sketch, "E79.3", {"start": v(-80, -80) * mm, "end": v(-80, 80) * mm});
            skArc(sketch, "E79.4", {"start": v(-80, -80) * mm, "mid": v(-77.07, -87.07) * mm, "end": v(-70, -90) * mm});
            skArc(sketch, "E79.5", {"start": v(70, -90) * mm, "mid": v(77.07, -87.07) * mm, "end": v(80, -80) * mm});
            skArc(sketch, "E79.6", {"start": v(80, 80) * mm, "mid": v(77.07, 87.07) * mm, "end": v(70, 90) * mm});
            skArc(sketch, "E79.7", {"start": v(-70, 90) * mm, "mid": v(-77.07, 87.07) * mm, "end": v(-80, 80) * mm});
            skArc(sketch, "E79.8", {"start": v(56.15, 48.18) * mm, "mid": v(0, 67.5) * mm, "end": v(-56.15, 48.18) * mm});
            skArc(sketch, "E79.9", {"start": v(-56.15, -48.18) * mm, "mid": v(0, -67.5) * mm, "end": v(56.15, -48.18) * mm});
            skLineSegment(sketch, "E79.10", {"start": v(-60, 40.3) * mm, "end": v(-60, -40.3) * mm});
            skArc(sketch, "E79.11", {"start": v(-60, -40.3) * mm, "mid": v(-58.99, -44.68) * mm, "end": v(-56.15, -48.18) * mm});
            skArc(sketch, "E79.12", {"start": v(-56.15, 48.18) * mm, "mid": v(-58.99, 44.68) * mm, "end": v(-60, 40.3) * mm});
            skLineSegment(sketch, "E79.13", {"start": v(60, 40.3) * mm, "end": v(60, -40.3) * mm});
            skArc(sketch, "E79.14", {"start": v(60, 40.3) * mm, "mid": v(58.99, 44.68) * mm, "end": v(56.15, 48.18) * mm});
            skArc(sketch, "E79.15", {"start": v(56.15, -48.18) * mm, "mid": v(58.99, -44.68) * mm, "end": v(60, -40.3) * mm});
            skCircle(sketch, "E79.16", {"center": v(60, -67.5) * mm, "radius": 4 * mm});
            skCircle(sketch, "E79.17", {"center": v(60, 67.5) * mm, "radius": 4 * mm});
            skCircle(sketch, "E79.18", {"center": v(-60, 67.5) * mm, "radius": 4 * mm});
            skCircle(sketch, "E79.19", {"center": v(-60, -67.5) * mm, "radius": 4 * mm});
            skLineSegment(sketch, "E80", {"start": v(0, 90) * mm, "end": v(0, 120) * mm, "construction": true});
            skLineSegment(sketch, "E81", {"start": v(-15, 108) * mm, "end": v(-33, 90) * mm});
            skLineSegment(sketch, "E82", {"start": v(15, 108) * mm, "end": v(33, 90) * mm});
            skLineSegment(sketch, "E83", {"start": v(-15, 108) * mm, "end": v(-15, 120) * mm});
            skLineSegment(sketch, "E84", {"start": v(15, 120) * mm, "end": v(15, 108) * mm});
            skArc(sketch, "E85", {"start": v(15, 120) * mm, "mid": v(0, 135) * mm, "end": v(-15, 120) * mm});
            skCircle(sketch, "E86", {"center": v(0, 120) * mm, "radius": 6 * mm});
            skLineSegment(sketch, "E87", {"start": v(-80, 0) * mm, "end": v(80, 0) * mm, "construction": true});
            skArc(sketch, "E88.MirrorCS", {"start": v(15, 104.25) * mm, "mid": v(0, 119.25) * mm, "end": v(-15, 104.25) * mm});
            skLineSegment(sketch, "E89.MirrorCS", {"start": v(15, -108) * mm, "end": v(33, -90) * mm});
            skLineSegment(sketch, "E90.MirrorCS", {"start": v(-15, -108) * mm, "end": v(-33, -90) * mm});
            skLineSegment(sketch, "E91.MirrorCS", {"start": v(-15, -108) * mm, "end": v(-15, -120) * mm});
            skLineSegment(sketch, "E92.MirrorCS", {"start": v(15, -120) * mm, "end": v(15, -108) * mm});
            skCircle(sketch, "E93.MirrorC", {"center": v(0, -120) * mm, "radius": 6 * mm});
            skLineSegment(sketch, "E94.MirrorCS", {"start": v(0, -90) * mm, "end": v(0, -120) * mm, "construction": true});
            skArc(sketch, "E95.MirrorCS", {"start": v(15, -120) * mm, "mid": v(0, -135) * mm, "end": v(-15, -120) * mm});
            skSolve(sketch);
        }
        {
            var Q0;
            {var subQ1=sQuery(id+"F16.wireOp",EDGE,"E81");Q0=makeQuery(id+"F16.imprint","IMPRINT",FACE,{"disambiguationData":[TD([[makeQuery(id+"F16.imprint","IMPRINT",EDGE,{"derivedFrom":subQ1}),1.0]])]});}
            var Q1;
            Q1=makeQuery(id+"F16.imprint","IMPRINT",FACE,{"disambiguationData":[TD([[makeQuery(id+"F16.imprint","IMPRINT",EDGE,{"derivedFrom":sQuery(id+"F16.wireOp",EDGE,"E79.0")}),1.0]])]});
            var Q2;
            {var subQ1=sQuery(id+"F16.wireOp",EDGE,"E89.MirrorCS");Q2=makeQuery(id+"F16.imprint","IMPRINT",FACE,{"disambiguationData":[TD([[makeQuery(id+"F16.imprint","IMPRINT",EDGE,{"derivedFrom":subQ1}),1.0]])]});}
            var Q3;
            Q3=makeQuery(id+"F2.opExtrude","CAP_FACE",FACE,{"disambiguationData":[OSD([sQuery(id+"F0.wireOp",EDGE,"E12"),sQuery(id+"F0.wireOp",EDGE,"E13"),sQuery(id+"F0.wireOp",EDGE,"E14"),sQuery(id+"F0.wireOp",EDGE,"E15"),sQuery(id+"F0.wireOp",EDGE,"E17.filletArc"),sQuery(id+"F0.wireOp",EDGE,"E18.filletArc"),sQuery(id+"F0.wireOp",EDGE,"E19.filletArc"),sQuery(id+"F0.wireOp",EDGE,"E20.filletArc"),sQuery(id+"F0.wireOp",EDGE,"E25.0"),sQuery(id+"F0.wireOp",EDGE,"E25.1"),sQuery(id+"F0.wireOp",EDGE,"E25.2"),sQuery(id+"F0.wireOp",EDGE,"E25.3"),sQuery(id+"F0.wireOp",EDGE,"E25.4"),sQuery(id+"F0.wireOp",EDGE,"E25.5"),sQuery(id+"F0.wireOp",EDGE,"E25.6"),sQuery(id+"F0.wireOp",EDGE,"E25.7")])],"isStart":false});
            extrude(context, id + "F17", {"entities" : qUnion([Q0, Q1, Q2]), "endBound" : BoundingType.UP_TO_SURFACE, "endBoundEntityFace" : qUnion([Q3]), "depth" : 25 * mm});
        }
    });
